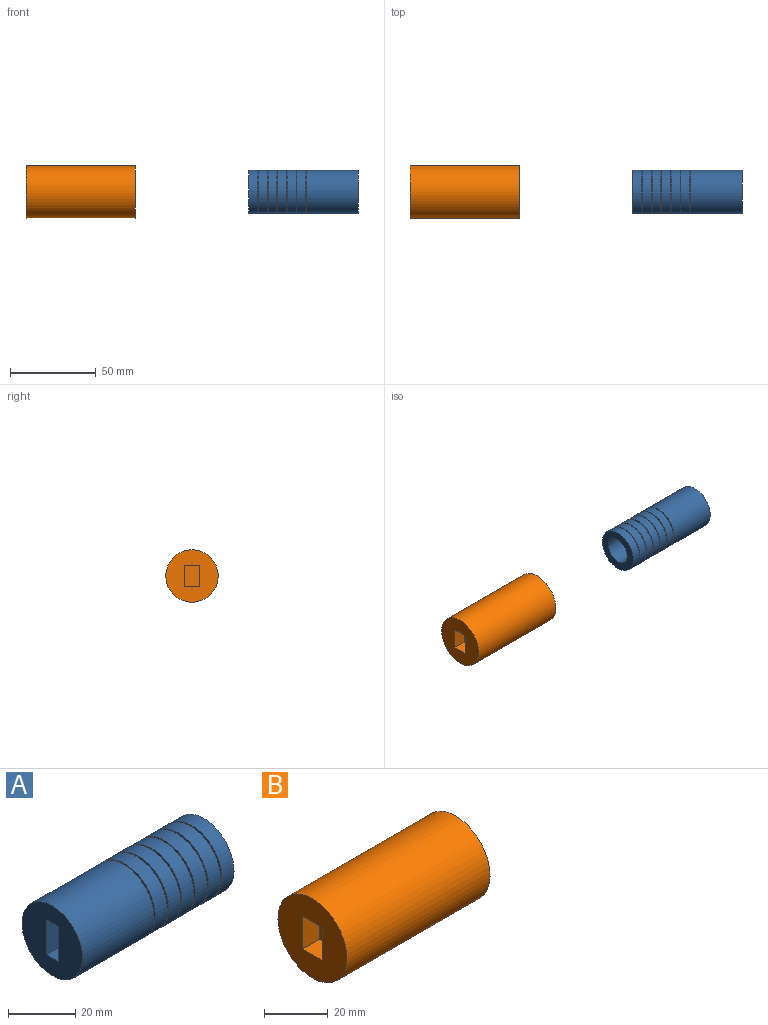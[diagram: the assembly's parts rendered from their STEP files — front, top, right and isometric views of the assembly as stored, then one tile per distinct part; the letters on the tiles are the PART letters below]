
ASSEMBLY  parts=2 mates=1
PART A: 34 faces, bbox 63.5x25.4x25.4 mm
  f0: plane 25.4x25.4mm, normal (-1,0,0), area 442.2mm2, adj f28,f29,f30,f31,f32
  f1: plane 15.24x15.24mm, normal (1,0,0), area 182.4mm2, adj f2
  f2: cylinder r=7.62mm len=50.8mm, axis (-1,0,0), area 2432.2mm2, adj f1,f3
  f3: plane 25.4x25.4mm, normal (1,0,0), area 324.3mm2, adj f2,f4
  f4: cylinder r=12.7mm len=25.4mm, axis (-1,0,0), area 405.4mm2, adj f3,f5
  f5: plane 25.4x25.4mm, normal (-1,0,0), area 96.3mm2, adj f4,f6
  f6: cylinder r=11.43mm len=22.86mm, axis (-1,0,0), area 36.5mm2, adj f5,f7
  f7: plane 25.4x25.4mm, normal (1,0,0), area 96.3mm2, adj f6,f8
  f8: cylinder r=12.7mm len=25.4mm, axis (-1,0,0), area 405.4mm2, adj f7,f9
  f9: plane 25.4x25.4mm, normal (-1,0,0), area 96.3mm2, adj f8,f10
  f10: cylinder r=11.43mm len=22.86mm, axis (-1,0,0), area 36.5mm2, adj f9,f11
  f11: plane 25.4x25.4mm, normal (1,0,0), area 96.3mm2, adj f10,f12
  f12: cylinder r=12.7mm len=25.4mm, axis (-1,0,0), area 405.4mm2, adj f11,f13
  f13: plane 25.4x25.4mm, normal (-1,0,0), area 96.3mm2, adj f12,f14
  f14: cylinder r=11.43mm len=22.86mm, axis (-1,0,0), area 36.5mm2, adj f13,f15
  f15: plane 25.4x25.4mm, normal (1,0,0), area 96.3mm2, adj f14,f16
  f16: cylinder r=12.7mm len=25.4mm, axis (-1,0,0), area 405.4mm2, adj f15,f17
  f17: plane 25.4x25.4mm, normal (-1,0,0), area 96.3mm2, adj f16,f18
  f18: cylinder r=11.43mm len=22.86mm, axis (-1,0,0), area 36.5mm2, adj f17,f19
  f19: plane 25.4x25.4mm, normal (1,0,0), area 96.3mm2, adj f18,f20
  f20: cylinder r=12.7mm len=25.4mm, axis (-1,0,0), area 405.4mm2, adj f19,f21
  f21: plane 25.4x25.4mm, normal (-1,0,0), area 96.3mm2, adj f20,f22
  f22: cylinder r=11.43mm len=22.86mm, axis (-1,0,0), area 36.5mm2, adj f21,f23
  f23: plane 25.4x25.4mm, normal (1,0,0), area 96.3mm2, adj f22,f24
  f24: cylinder r=12.7mm len=25.4mm, axis (-1,0,0), area 405.4mm2, adj f23,f25
  f25: plane 25.4x25.4mm, normal (-1,0,0), area 96.3mm2, adj f24,f26
  f26: cylinder r=11.43mm len=22.86mm, axis (-1,0,0), area 36.5mm2, adj f25,f27
  f27: plane 25.4x25.4mm, normal (1,0,0), area 96.3mm2, adj f26,f28
  f28: cylinder r=12.7mm len=29.97mm, axis (-1,0,0), area 2391.7mm2, adj f0,f27
  f29: plane 12.7x7.62mm, normal (0,-1,0), area 96.8mm2, adj f0,f30,f32,f33
  f30: plane 7.62x5.08mm, normal (0,0,1), area 38.7mm2, adj f0,f29,f31,f33
  f31: plane 12.7x7.62mm, normal (0,1,0), area 96.8mm2, adj f0,f30,f32,f33
  f32: plane 7.62x5.08mm, normal (0,0,-1), area 38.7mm2, adj f0,f29,f31,f33
  f33: plane 12.7x5.08mm, normal (-1,0,0), area 64.5mm2, adj f29,f30,f31,f32
PART B: 12 faces, bbox 63.5x30.5x30.5 mm
  f0: plane 30.48x30.48mm, normal (-1,0,0), area 616.8mm2, adj f6,f7,f8,f9,f10
  f1: plane 15.24x15.24mm, normal (1,0,0), area 182.4mm2, adj f2
  f2: cylinder r=7.62mm len=15.24mm, axis (-1,0,0), area 243.2mm2, adj f1,f3
  f3: plane 25.4x25.4mm, normal (1,0,0), area 324.3mm2, adj f2,f4
  f4: cylinder r=12.7mm len=45.72mm, axis (-1,0,0), area 3648.3mm2, adj f3,f5
  f5: plane 30.48x30.48mm, normal (1,0,0), area 223mm2, adj f4,f6
  f6: cylinder r=15.24mm len=63.5mm, axis (-1,0,0), area 6080.5mm2, adj f0,f5
  f7: plane 8.89x7.62mm, normal (0,0,-1), area 67.7mm2, adj f0,f8,f10,f11
  f8: plane 12.7x7.62mm, normal (0,-1,0), area 96.8mm2, adj f0,f7,f9,f11
  f9: plane 8.89x7.62mm, normal (0,0,1), area 67.7mm2, adj f0,f8,f10,f11
  f10: plane 12.7x7.62mm, normal (0,1,0), area 96.8mm2, adj f0,f7,f9,f11
  f11: plane 12.7x8.89mm, normal (-1,0,0), area 112.9mm2, adj f7,f8,f9,f10
PLACE A rot(axis=(0,1,0),180deg) t=(96.07,-67.51,-17.03)mm
PLACE B t=(-97.27,-67.51,-17.03)mm fixed
MATE slider A.f2 <-> B.f2  axis (1,0,0) through (96.07,-67.51,-17.03)mm
